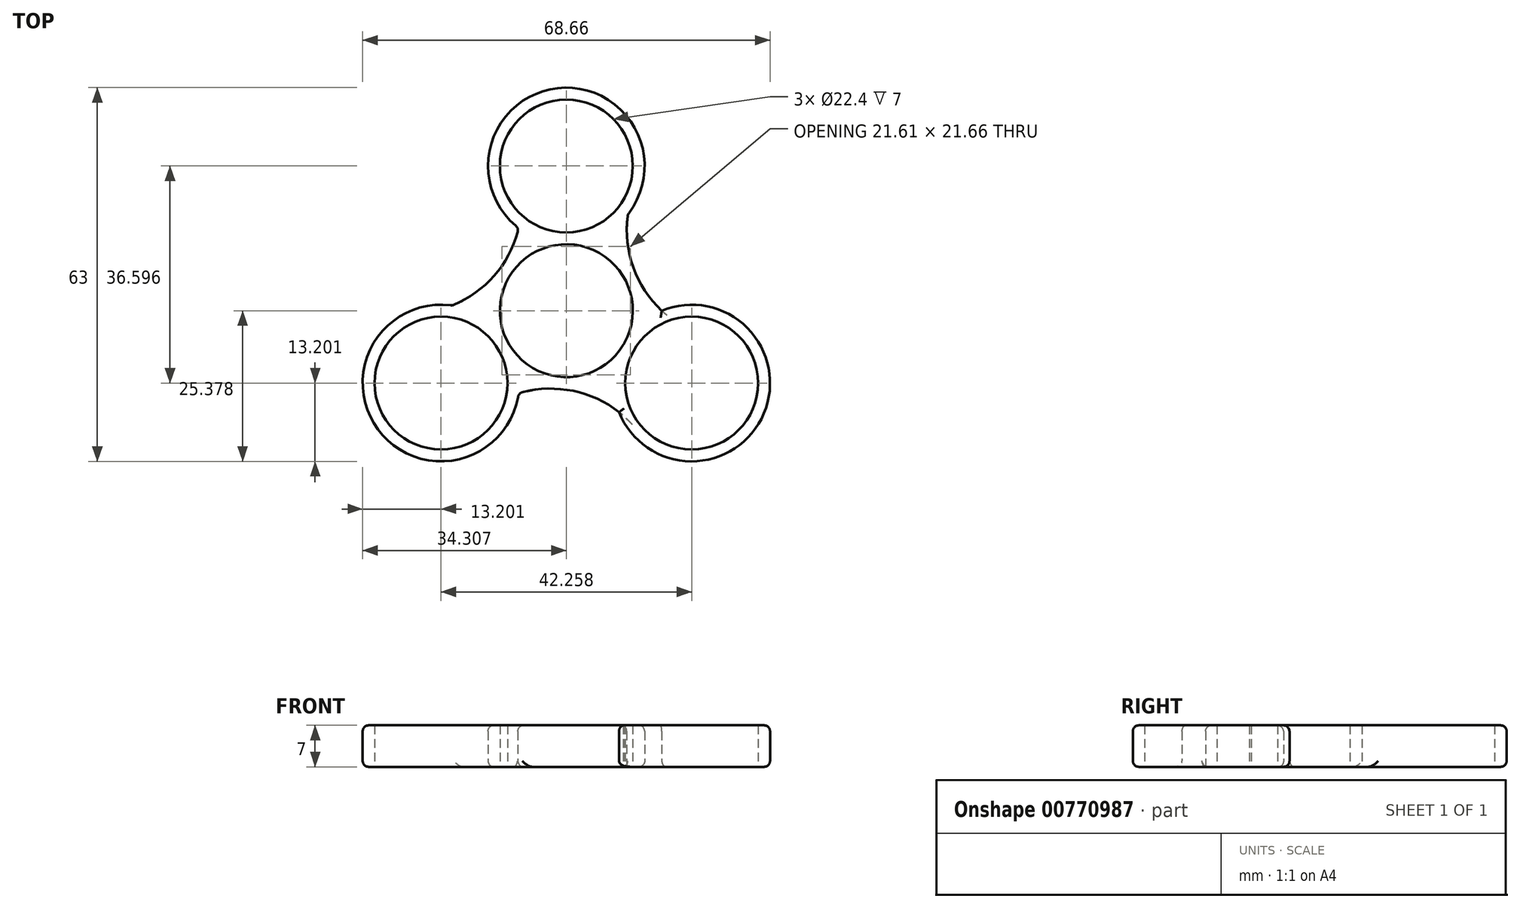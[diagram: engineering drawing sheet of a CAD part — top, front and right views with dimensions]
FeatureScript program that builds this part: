
annotation { "Feature Type Name" : "Feature", "Feature Type Description" : "" }
export const myFeature = defineFeature(function(context is Context, id is Id, definition is map)
    precondition{}
    {
        {
            var Q0;
            Q0=qCreatedBy(makeId("Top.planeOp"),FACE);
            var sketch = newSketch(context, id + "F0", { "sketchPlane" : qUnion([Q0])});
            skArc(sketch, "E0", {"start": v(9.79, -5.45) * mm, "mid": v(-9.7, 5.6) * mm, "end": v(9.61, -5.75) * mm});
            skArc(sketch, "E1", {"start": v(0.18, 13.2) * mm, "mid": v(0, 13.2) * mm, "end": v(-0.18, 13.2) * mm});
            skCircle(sketch, "E2", {"center": v(0, 24.4) * mm, "radius": 11.2 * mm});
            skArc(sketch, "E3", {"start": v(10.38, 16.24) * mm, "mid": v(-1.64, 37.5) * mm, "end": v(-8.04, 13.93) * mm});
            skCircle(sketch, "E4.1.0", {"center": v(-21.13, -12.2) * mm, "radius": 11.2 * mm});
            skArc(sketch, "E4.1.1", {"start": v(-19.25, 0.87) * mm, "mid": v(-31.65, -20.17) * mm, "end": v(-8.04, -13.93) * mm});
            skCircle(sketch, "E4.2.0", {"center": v(21.13, -12.2) * mm, "radius": 11.2 * mm});
            skArc(sketch, "E4.2.1", {"start": v(8.88, -17.1) * mm, "mid": v(33.3, -17.33) * mm, "end": v(16.09, 0) * mm});
            skArc(sketch, "E5", {"start": v(10.38, 16.24) * mm, "mid": v(11.25, 7.42) * mm, "end": v(16.09, 0) * mm});
            skArc(sketch, "E6.1.0", {"start": v(-19.25, 0.87) * mm, "mid": v(-12.05, 6.03) * mm, "end": v(-8.04, 13.93) * mm});
            skArc(sketch, "E6.2.0", {"start": v(8.88, -17.1) * mm, "mid": v(0.8, -13.45) * mm, "end": v(-8.04, -13.93) * mm});
            skArc(sketch, "E7.trimOffspring", {"start": v(-11.52, -6.45) * mm, "mid": v(-11.43, -6.6) * mm, "end": v(-11.34, -6.75) * mm});
            skArc(sketch, "E8.trimOffspring", {"start": v(-0.18, 11.2) * mm, "mid": v(0, 11.2) * mm, "end": v(0.18, 11.2) * mm});
            skArc(sketch, "E9.trimOffspring", {"start": v(-9.61, -5.75) * mm, "mid": v(-9.7, -5.6) * mm, "end": v(-9.79, -5.45) * mm});
            skArc(sketch, "E10.trimOffspring", {"start": v(11.34, -6.75) * mm, "mid": v(11.43, -6.6) * mm, "end": v(11.52, -6.45) * mm});
            skArc(sketch, "E11.trimOffspring", {"start": v(9.79, -5.45) * mm, "mid": v(9.7, -5.6) * mm, "end": v(9.61, -5.75) * mm});
            skSolve(sketch);
        }
        {
            var Q0;
            Q0=makeQuery(id+"F0.imprint","IMPRINT",FACE,{"disambiguationData":[TD([[makeQuery(id+"F0.imprint","IMPRINT",EDGE,{"derivedFrom":sQuery(id+"F0.wireOp",EDGE,"E3")}),1.0]])]});
            extrude(context, id + "F1", {"entities" : qUnion([Q0]), "depth" : 7 * mm, "offsetDistance" : 25 * mm});
        }
        {
            var Q0;
            Q0=makeQuery(id+"F1.opExtrude","CAP_EDGE",EDGE,{"disambiguationData":[OSD([sQuery(id+"F0.wireOp",EDGE,"E3")])],"isStart":false});
            var Q1;
            Q1=makeQuery(id+"F1.opExtrude","CAP_EDGE",EDGE,{"disambiguationData":[OSD([sQuery(id+"F0.wireOp",EDGE,"E6.1.0")])],"isStart":false});
            var Q2;
            Q2=makeQuery(id+"F1.opExtrude","CAP_EDGE",EDGE,{"disambiguationData":[OSD([sQuery(id+"F0.wireOp",EDGE,"E4.1.1")])],"isStart":false});
            var Q3;
            Q3=makeQuery(id+"F1.opExtrude","CAP_EDGE",EDGE,{"disambiguationData":[OSD([sQuery(id+"F0.wireOp",EDGE,"E6.2.0")])],"isStart":false});
            var Q4;
            Q4=makeQuery(id+"F1.opExtrude","CAP_EDGE",EDGE,{"disambiguationData":[OSD([sQuery(id+"F0.wireOp",EDGE,"E4.2.1")])],"isStart":false});
            var Q5;
            Q5=makeQuery(id+"F1.opExtrude","CAP_EDGE",EDGE,{"disambiguationData":[OSD([sQuery(id+"F0.wireOp",EDGE,"E5")])],"isStart":false});
            var Q6;
            Q6=makeQuery(id+"F1.opExtrude","SWEPT_FACE",FACE,{"disambiguationData":[OSD([sQuery(id+"F0.wireOp",EDGE,"E4.1.1")])]});
            var Q7;
            Q7=makeQuery(id+"F1.opExtrude","SWEPT_FACE",FACE,{"disambiguationData":[OSD([sQuery(id+"F0.wireOp",EDGE,"E3")])]});
            var Q8;
            Q8=makeQuery(id+"F1.opExtrude","CAP_EDGE",EDGE,{"disambiguationData":[OSD([sQuery(id+"F0.wireOp",EDGE,"E4.2.1")])],"isStart":true});
            fillet(context, id + "F2", {"entities" : qUnion([Q0, Q1, Q2, Q3, Q4, Q5, Q6, Q7, Q8]), "radius" : 1 * mm, "tangentPropagation" : true, "allowEdgeOverflow" : false});
        }
    });
